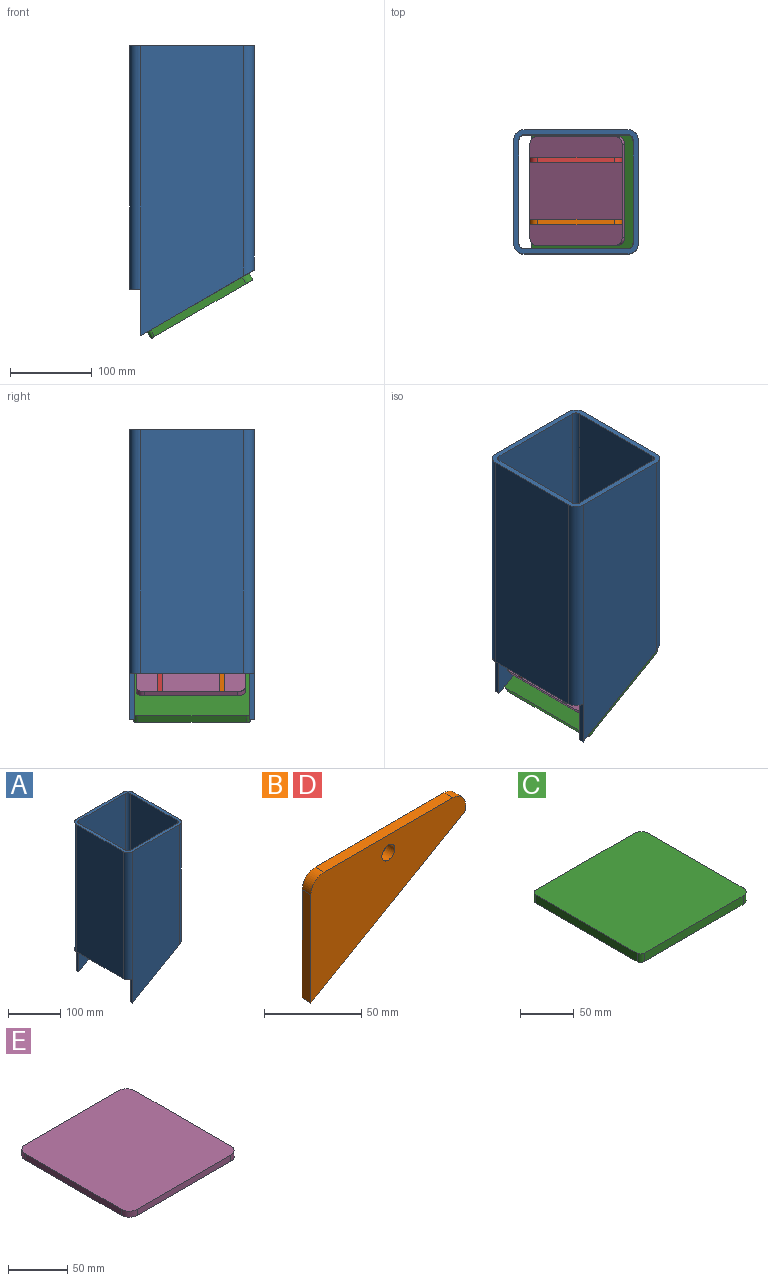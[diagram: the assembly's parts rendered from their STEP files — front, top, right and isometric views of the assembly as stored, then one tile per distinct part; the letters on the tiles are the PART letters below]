
ASSEMBLY  parts=5 mates=4
PART A: 21 faces, bbox 152.4x152.4x355.6 mm
  f0: plane 274.94x127mm, normal (1,0,0), area 34917.9mm2, adj f1,f8,f16,f20
  f1: cylinder r=12.7mm len=282.28mm, axis (0,0,-1), area 5538mm2, adj f0,f2,f16,f20
  f2: plane 355.6x127mm, normal (0,1,0), area 40505.2mm2, adj f1,f9,f16,f18,f20
  f3: plane 355.6x127mm, normal (0,-1,0), area 40505.2mm2, adj f4,f11,f16,f18,f20
  f4: cylinder r=6.35mm len=282.28mm, axis (0,0,-1), area 2792.3mm2, adj f3,f5,f16,f20
  f5: plane 278.61x127mm, normal (-1,0,0), area 35383.5mm2, adj f4,f6,f16,f20
  f6: cylinder r=6.35mm len=282.28mm, axis (0,0,-1), area 2792.3mm2, adj f5,f7,f16,f20
  f7: plane 355.6x127mm, normal (0,1,0), area 40505.2mm2, adj f6,f12,f16,f19,f20
  f8: cylinder r=12.7mm len=282.28mm, axis (0,0,-1), area 5538mm2, adj f0,f15,f16,f20
  f9: cylinder r=12.7mm len=298.49mm, axis (0,0,-1), area 5954.6mm2, adj f2,f14,f16,f17
  f10: cylinder r=12.7mm len=298.49mm, axis (0,0,-1), area 5954.6mm2, adj f14,f15,f16,f17
  f11: cylinder r=6.35mm len=298.49mm, axis (0,0,-1), area 2977.3mm2, adj f3,f13,f16,f17
  f12: cylinder r=6.35mm len=298.49mm, axis (0,0,-1), area 2977.3mm2, adj f7,f13,f16,f17
  f13: plane 298.49x127mm, normal (1,0,0), area 37908mm2, adj f11,f12,f16,f17
  f14: plane 298.49x127mm, normal (-1,0,0), area 37908mm2, adj f9,f10,f16,f17
  f15: plane 355.6x127mm, normal (0,-1,0), area 40505.2mm2, adj f8,f10,f16,f19,f20
  f16: plane 152.4x152.4mm, normal (0,0,1), area 3605.8mm2, adj f0,f1,f2,f3,f4,f5,f6,f7
  f17: plane 152.4x12.7mm, normal (0,0,-1), area 996.5mm2, adj f9,f10,f11,f12,f13,f14,f18,f19
  f18: plane 57.11x6.35mm, normal (-1,0,0), area 362.7mm2, adj f2,f3,f17,f20
  f19: plane 57.11x6.35mm, normal (-1,0,0), area 362.7mm2, adj f7,f15,f17,f20
  f20: plane 152.4x139.7mm, normal (0.5,0,-0.87), area 3013mm2, adj f0,f1,f2,f3,f4,f5,f6,f7
PART B: 9 faces, bbox 112.7x6.4x77.8 mm
  f0: plane 112.74x65.09mm, normal (0.5,0,-0.87), area 826.6mm2, adj f1,f5,f6,f7
  f1: plane 6.35x3.18mm, normal (1,0,0), area 20.2mm2, adj f0,f2,f6,f7
  f2: cylinder r=9.53mm len=9.53mm, axis (0,1,0), area 95mm2, adj f1,f3,f6,f7
  f3: plane 93.69x6.35mm, normal (0,0,1), area 594.9mm2, adj f2,f4,f6,f7
  f4: cylinder r=9.53mm len=9.53mm, axis (0,1,0), area 95mm2, adj f3,f5,f6,f7
  f5: plane 68.26x6.35mm, normal (-1,0,0), area 433.5mm2, adj f0,f4,f6,f7
  f6: plane 112.74x77.79mm, normal (0,-1,0), area 4990.4mm2, adj f0,f1,f2,f3,f4,f5,f8
  f7: plane 112.74x77.79mm, normal (0,1,0), area 4990.4mm2, adj f0,f1,f2,f3,f4,f5,f8
  f8: cylinder r=4.76mm len=9.53mm, axis (0,-1,0), area 190mm2, adj f6,f7
PART C: 10 faces, bbox 143.8x142.9x9.5 mm
  f0: plane 129.5x9.53mm, normal (0,-1,0), area 1233.5mm2, adj f1,f7,f8,f9
  f1: cylinder r=9.53mm len=9.53mm, axis (0,0,-1), area 142.5mm2, adj f0,f2,f8,f9
  f2: plane 123.83x9.53mm, normal (1,0,0), area 1179.4mm2, adj f1,f3,f8,f9
  f3: cylinder r=9.53mm len=9.53mm, axis (0,0,-1), area 142.5mm2, adj f2,f4,f8,f9
  f4: plane 129.5x9.53mm, normal (0,1,0), area 1233.5mm2, adj f3,f5,f8,f9
  f5: cylinder r=4.83mm len=9.53mm, axis (0,0,-1), area 72.2mm2, adj f4,f6,f8,f9
  f6: plane 133.22x9.53mm, normal (-1,0,0), area 1268.9mm2, adj f5,f7,f8,f9
  f7: cylinder r=4.83mm len=9.53mm, axis (0,0,-1), area 72.2mm2, adj f0,f6,f8,f9
  f8: plane 143.85x142.88mm, normal (0,0,1), area 20503.5mm2, adj f0,f1,f2,f3,f4,f5,f6,f7
  f9: plane 143.85x142.88mm, normal (0,0,-1), area 20503.5mm2, adj f0,f1,f2,f3,f4,f5,f6,f7
PART D: same geometry as B
PART E: 10 faces, bbox 130.6x133.4x6.4 mm
  f0: plane 111.51x6.35mm, normal (0,1,0), area 708.1mm2, adj f1,f7,f8,f9
  f1: cylinder r=9.53mm len=9.53mm, axis (0,0,-1), area 95mm2, adj f0,f2,f8,f9
  f2: plane 114.3x6.35mm, normal (-1,0,0), area 725.8mm2, adj f1,f3,f8,f9
  f3: cylinder r=9.53mm len=9.53mm, axis (0,0,-1), area 95mm2, adj f2,f4,f8,f9
  f4: plane 111.51x6.35mm, normal (0,-1,0), area 708.1mm2, adj f3,f5,f8,f9
  f5: cylinder r=9.53mm len=9.53mm, axis (0,0,-1), area 95mm2, adj f4,f6,f8,f9
  f6: plane 114.3x6.35mm, normal (1,0,0), area 725.8mm2, adj f5,f7,f8,f9
  f7: cylinder r=9.53mm len=9.53mm, axis (0,0,-1), area 95mm2, adj f0,f6,f8,f9
  f8: plane 133.35x130.56mm, normal (0,0,1), area 17331.8mm2, adj f0,f1,f2,f3,f4,f5,f6,f7
  f9: plane 133.35x130.56mm, normal (0,0,-1), area 17331.8mm2, adj f0,f1,f2,f3,f4,f5,f6,f7
PLACE A t=(4.09,18.36,-355.6)mm
PLACE B t=(-66.39,29.97,-315.72)mm
PLACE C rot(axis=(-0.97,0,-0.26),180deg) t=(-14.93,133.35,-283.56)mm
PLACE D t=(-66.39,106.17,-315.72)mm
PLACE E rot(axis=(0.97,0,0.26),180deg) t=(-10.21,129.79,-250.03)mm
MATE planar C.f9 <-> A.f20  axis (-0.5,0,0.87) through (-6.35,63.5,-278.61)mm
MATE fastened E.f9 <-> B.f0  axis (-0.5,0,0.87) through (-76.2,-1.78,-288.13)mm
MATE fastened D.f0 <-> E.f9  axis (0.5,0,-0.87) through (-76.2,106.17,-288.13)mm
MATE planar A.f7 <-> B.f8  axis (0,1,0) through (-76.2,-6.35,0)mm
